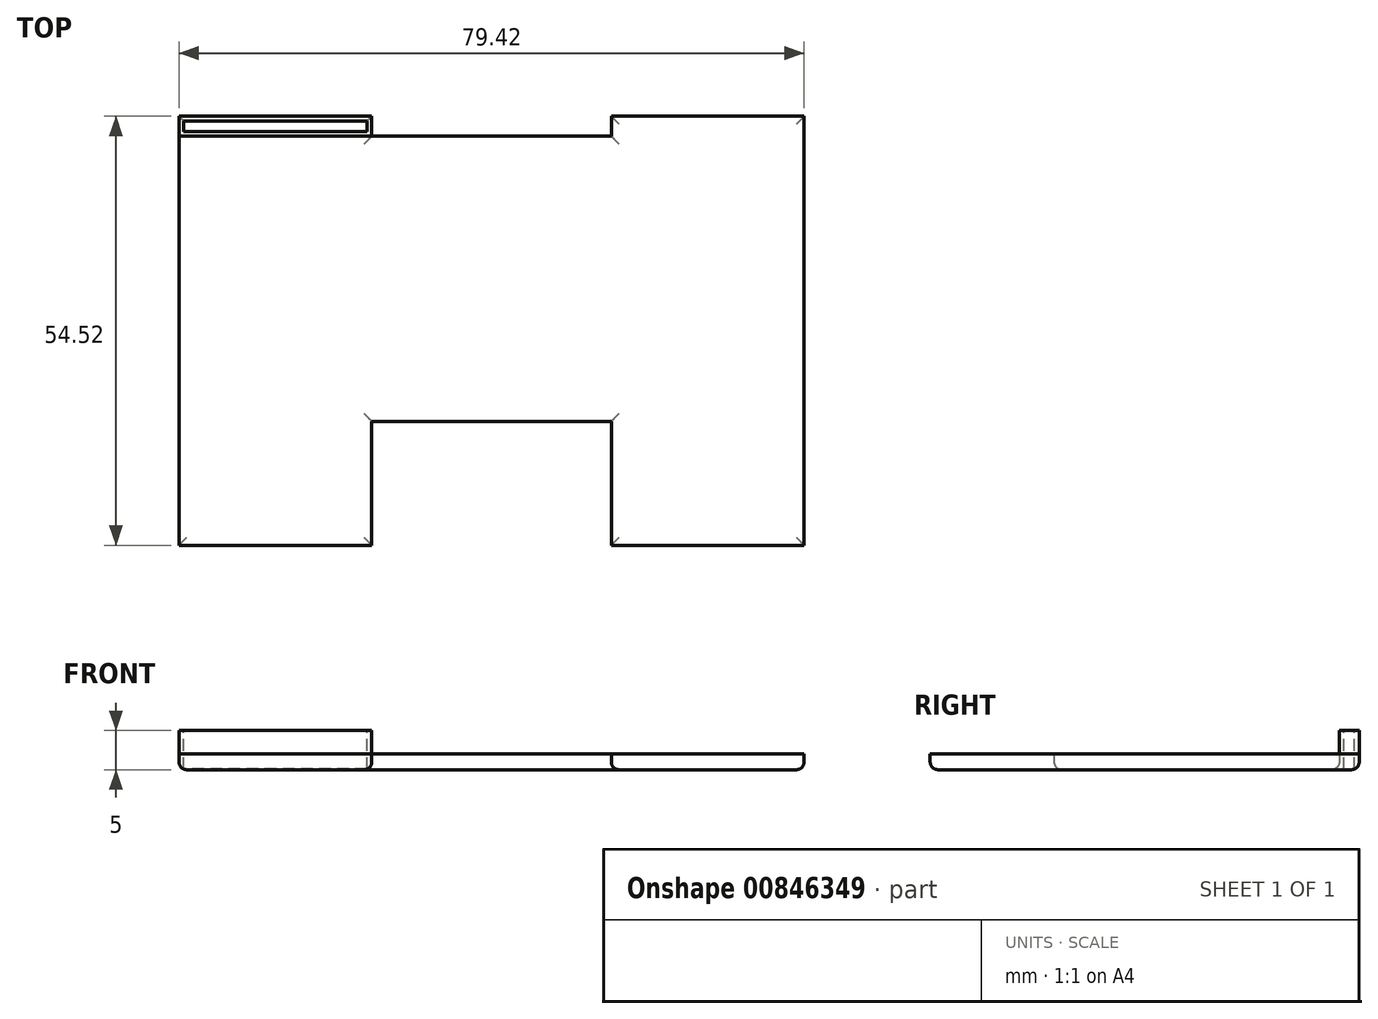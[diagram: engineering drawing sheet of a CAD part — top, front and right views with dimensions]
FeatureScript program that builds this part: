
annotation { "Feature Type Name" : "Feature", "Feature Type Description" : "" }
export const myFeature = defineFeature(function(context is Context, id is Id, definition is map)
    precondition{}
    {
        {
            var Q0;
            Q0=qCreatedBy(makeId("Top.planeOp"),FACE);
            var sketch = newSketch(context, id + "F0", { "sketchPlane" : qUnion([Q0])});
            skLineSegment(sketch, "E0", {"start": v(25.15, 27.9) * mm, "end": v(25.15, -26.6) * mm});
            skLineSegment(sketch, "E1", {"start": v(25.15, -26.6) * mm, "end": v(0.65, -26.6) * mm});
            skLineSegment(sketch, "E2", {"start": v(-54.27, -26.6) * mm, "end": v(-54.27, 27.9) * mm});
            skLineSegment(sketch, "E3", {"start": v(-54.27, 27.9) * mm, "end": v(-29.77, 27.9) * mm});
            skLineSegment(sketch, "E4", {"start": v(-29.77, 27.9) * mm, "end": v(-29.77, 25.38) * mm});
            skLineSegment(sketch, "E5", {"start": v(-29.77, 25.38) * mm, "end": v(0.65, 25.38) * mm});
            skLineSegment(sketch, "E6", {"start": v(0.65, 25.38) * mm, "end": v(0.65, 27.9) * mm});
            skLineSegment(sketch, "E7", {"start": v(0.65, 27.9) * mm, "end": v(25.15, 27.9) * mm});
            skLineSegment(sketch, "E8", {"start": v(-29.77, -10.86) * mm, "end": v(0.65, -10.86) * mm});
            skLineSegment(sketch, "E9", {"start": v(-29.77, -10.86) * mm, "end": v(-29.77, -26.6) * mm});
            skLineSegment(sketch, "E10", {"start": v(0.65, -10.86) * mm, "end": v(0.65, -26.6) * mm});
            skLineSegment(sketch, "E11.trimOffspring", {"start": v(-29.77, -26.6) * mm, "end": v(-54.27, -26.6) * mm});
            skSolve(sketch);
        }
        {
            var Q0;
            Q0 = qSketchRegion(id + "F0", true);
            extrude(context, id + "F1", {"entities" : qUnion([Q0]), "depth" : 2 * mm, "offsetDistance" : 25 * mm});
        }
        {
            var Q0;
            Q0=makeQuery(id+"F1.opExtrude","CAP_FACE",FACE,{"disambiguationData":[OSD([sQuery(id+"F0.wireOp",EDGE,"E0"),sQuery(id+"F0.wireOp",EDGE,"E1"),sQuery(id+"F0.wireOp",EDGE,"E2"),sQuery(id+"F0.wireOp",EDGE,"E3"),sQuery(id+"F0.wireOp",EDGE,"E4"),sQuery(id+"F0.wireOp",EDGE,"E5"),sQuery(id+"F0.wireOp",EDGE,"E6"),sQuery(id+"F0.wireOp",EDGE,"E7"),sQuery(id+"F0.wireOp",EDGE,"E8"),sQuery(id+"F0.wireOp",EDGE,"E9"),sQuery(id+"F0.wireOp",EDGE,"E10"),sQuery(id+"F0.wireOp",EDGE,"E11.trimOffspring")])],"isStart":false});
            var sketch = newSketch(context, id + "F2", { "sketchPlane" : qUnion([Q0])});
            skLineSegment(sketch, "E12", {"start": v(-29.77, 25.38) * mm, "end": v(-54.27, 25.38) * mm});
            skLineSegment(sketch, "E13", {"start": v(-54.27, 25.38) * mm, "end": v(-54.27, 27.9) * mm});
            skLineSegment(sketch, "E14", {"start": v(-54.27, 27.9) * mm, "end": v(-29.77, 27.9) * mm});
            skLineSegment(sketch, "E15", {"start": v(-29.77, 27.9) * mm, "end": v(-29.77, 25.38) * mm});
            skLineSegment(sketch, "E16.0", {"start": v(-30.37, 27.3) * mm, "end": v(-30.37, 25.98) * mm});
            skLineSegment(sketch, "E16.1", {"start": v(-53.67, 27.3) * mm, "end": v(-30.37, 27.3) * mm});
            skLineSegment(sketch, "E16.2", {"start": v(-53.67, 25.98) * mm, "end": v(-53.67, 27.3) * mm});
            skLineSegment(sketch, "E16.3", {"start": v(-30.37, 25.98) * mm, "end": v(-53.67, 25.98) * mm});
            skSolve(sketch);
        }
        {
            var Q0;
            Q0 = qSketchRegion(id + "F0", true);
            var Q1;
            Q1=makeQuery(id+"F2.imprint","IMPRINT",FACE,{"disambiguationData":[TD([[makeQuery(id+"F2.imprint","IMPRINT",EDGE,{"derivedFrom":sQuery(id+"F2.wireOp",EDGE,"E16.0")}),-1.0]])]});
            extrude(context, id + "F3", {"entities" : qUnion([Q0, Q1]), "operationType" : NewBodyOperationType.REMOVE, "oppositeDirection" : true, "depth" : 2 * mm, "offsetDistance" : 25 * mm});
        }
        {
            var Q0;
            Q0 = qSketchRegion(id + "F2", true);
            extrude(context, id + "F4", {"entities" : qUnion([Q0]), "operationType" : NewBodyOperationType.ADD, "depth" : 3 * mm, "offsetDistance" : 25 * mm});
        }
        {
            var Q0;
            Q0=makeQuery(id+"F1.opExtrude","CAP_EDGE",EDGE,{"disambiguationData":[OSD([sQuery(id+"F0.wireOp",EDGE,"E11.trimOffspring")])],"isStart":true});
            var Q1;
            Q1=makeQuery(id+"F1.opExtrude","CAP_EDGE",EDGE,{"disambiguationData":[OSD([sQuery(id+"F0.wireOp",EDGE,"E2")])],"isStart":true});
            var Q2;
            Q2=makeQuery(id+"F1.opExtrude","CAP_EDGE",EDGE,{"disambiguationData":[OSD([sQuery(id+"F0.wireOp",EDGE,"E3")])],"isStart":true});
            var Q3;
            Q3=makeQuery(id+"F1.opExtrude","CAP_EDGE",EDGE,{"disambiguationData":[OSD([sQuery(id+"F0.wireOp",EDGE,"E4")])],"isStart":true});
            var Q4;
            Q4=makeQuery(id+"F1.opExtrude","CAP_EDGE",EDGE,{"disambiguationData":[OSD([sQuery(id+"F0.wireOp",EDGE,"E5")])],"isStart":true});
            var Q5;
            Q5=makeQuery(id+"F1.opExtrude","CAP_EDGE",EDGE,{"disambiguationData":[OSD([sQuery(id+"F0.wireOp",EDGE,"E9")])],"isStart":true});
            var Q6;
            Q6=makeQuery(id+"F1.opExtrude","CAP_EDGE",EDGE,{"disambiguationData":[OSD([sQuery(id+"F0.wireOp",EDGE,"E8")])],"isStart":true});
            var Q7;
            Q7=makeQuery(id+"F1.opExtrude","CAP_EDGE",EDGE,{"disambiguationData":[OSD([sQuery(id+"F0.wireOp",EDGE,"E10")])],"isStart":true});
            var Q8;
            Q8=makeQuery(id+"F1.opExtrude","CAP_EDGE",EDGE,{"disambiguationData":[OSD([sQuery(id+"F0.wireOp",EDGE,"E1")])],"isStart":true});
            var Q9;
            Q9=makeQuery(id+"F1.opExtrude","CAP_EDGE",EDGE,{"disambiguationData":[OSD([sQuery(id+"F0.wireOp",EDGE,"E0")])],"isStart":true});
            var Q10;
            Q10=makeQuery(id+"F1.opExtrude","CAP_EDGE",EDGE,{"disambiguationData":[OSD([sQuery(id+"F0.wireOp",EDGE,"E7")])],"isStart":true});
            var Q11;
            Q11=makeQuery(id+"F1.opExtrude","CAP_EDGE",EDGE,{"disambiguationData":[OSD([sQuery(id+"F0.wireOp",EDGE,"E6")])],"isStart":true});
            fillet(context, id + "F5", {"entities" : qUnion([Q0, Q1, Q2, Q3, Q4, Q5, Q6, Q7, Q8, Q9, Q10, Q11]), "radius" : 1 * mm, "tangentPropagation" : true, "allowEdgeOverflow" : false});
        }
    });
